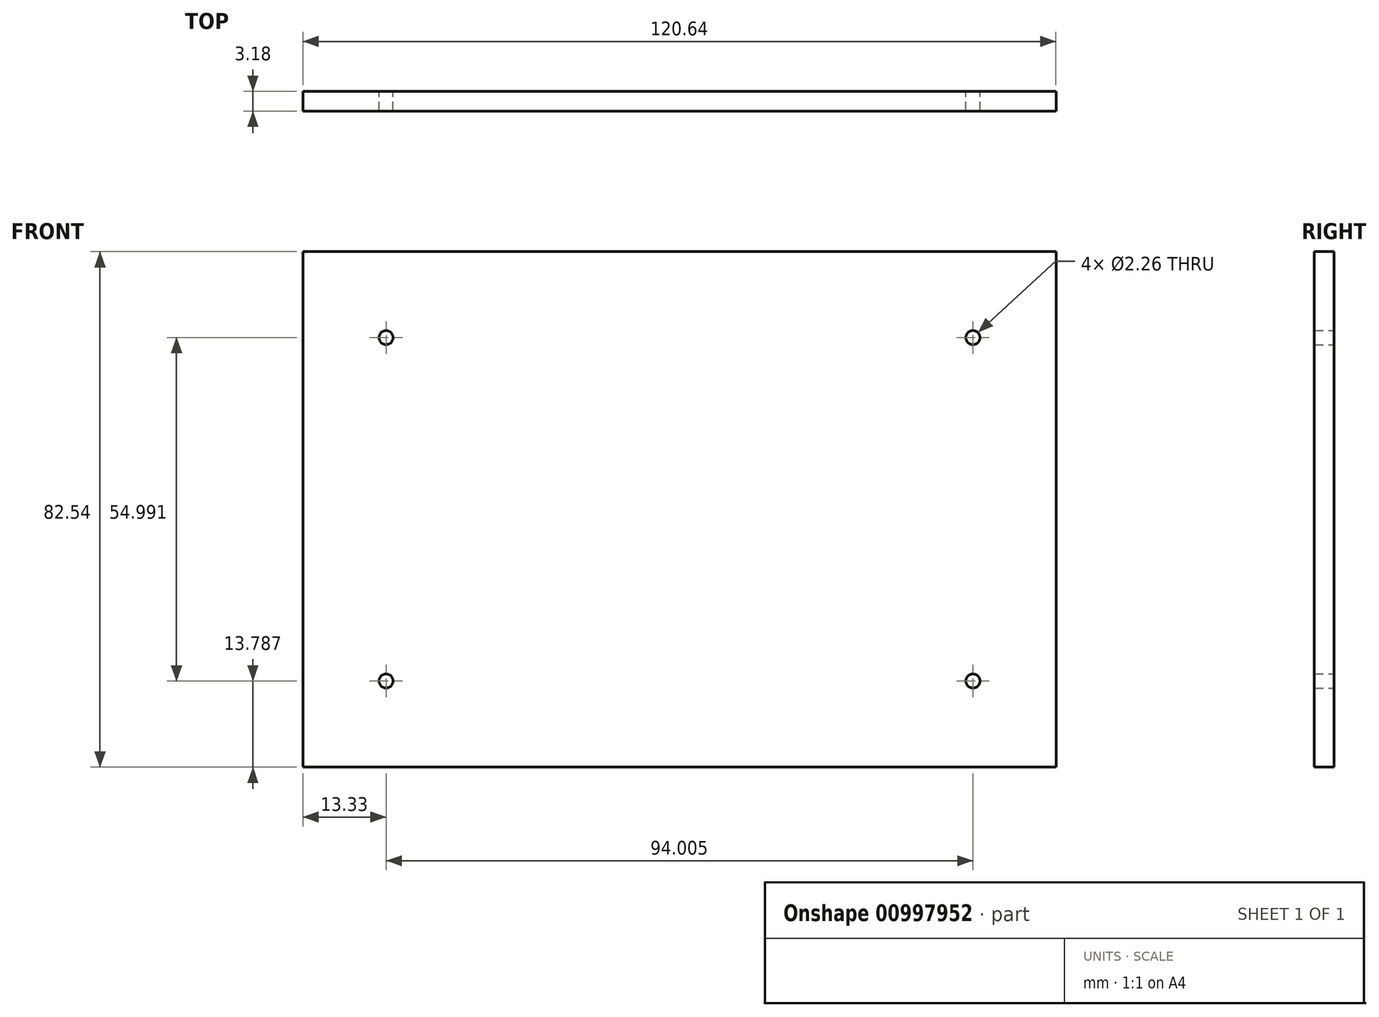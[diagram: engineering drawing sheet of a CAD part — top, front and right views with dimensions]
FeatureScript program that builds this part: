
annotation { "Feature Type Name" : "Feature", "Feature Type Description" : "" }
export const myFeature = defineFeature(function(context is Context, id is Id, definition is map)
    precondition{}
    {
        {
            var Q0;
            Q0=qCreatedBy(makeId("Front.planeOp"),FACE);
            var sketch = newSketch(context, id + "F0", { "sketchPlane" : qUnion([Q0])});
            skLineSegment(sketch, "E0.bottom", {"start": v(-60.33, 41.27) * mm, "end": v(60.33, 41.28) * mm});
            skLineSegment(sketch, "E0.top", {"start": v(-60.33, -41.27) * mm, "end": v(60.33, -41.27) * mm});
            skLineSegment(sketch, "E0.left", {"start": v(-60.33, 41.27) * mm, "end": v(-60.33, -41.27) * mm});
            skLineSegment(sketch, "E0.right", {"start": v(60.33, 41.28) * mm, "end": v(60.33, -41.27) * mm});
            skCircle(sketch, "E1", {"center": v(-47, 27.5) * mm, "radius": 1.13 * mm});
            skCircle(sketch, "E2", {"center": v(47.02, 27.5) * mm, "radius": 1.13 * mm});
            skCircle(sketch, "E3", {"center": v(47.02, -27.48) * mm, "radius": 1.13 * mm});
            skCircle(sketch, "E4", {"center": v(-47, -27.48) * mm, "radius": 1.13 * mm});
            skSolve(sketch);
        }
        {
            var Q0;
            Q0=makeQuery(id+"F0.imprint","IMPRINT",FACE,{"disambiguationData":[TD([[makeQuery(id+"F0.imprint","IMPRINT",EDGE,{"derivedFrom":sQuery(id+"F0.wireOp",EDGE,"E0.bottom")}),-1.0]])]});
            extrude(context, id + "F1", {"entities" : qUnion([Q0]), "depth" : 3.17 * mm, "offsetDistance" : 25.4 * mm});
        }
    });
